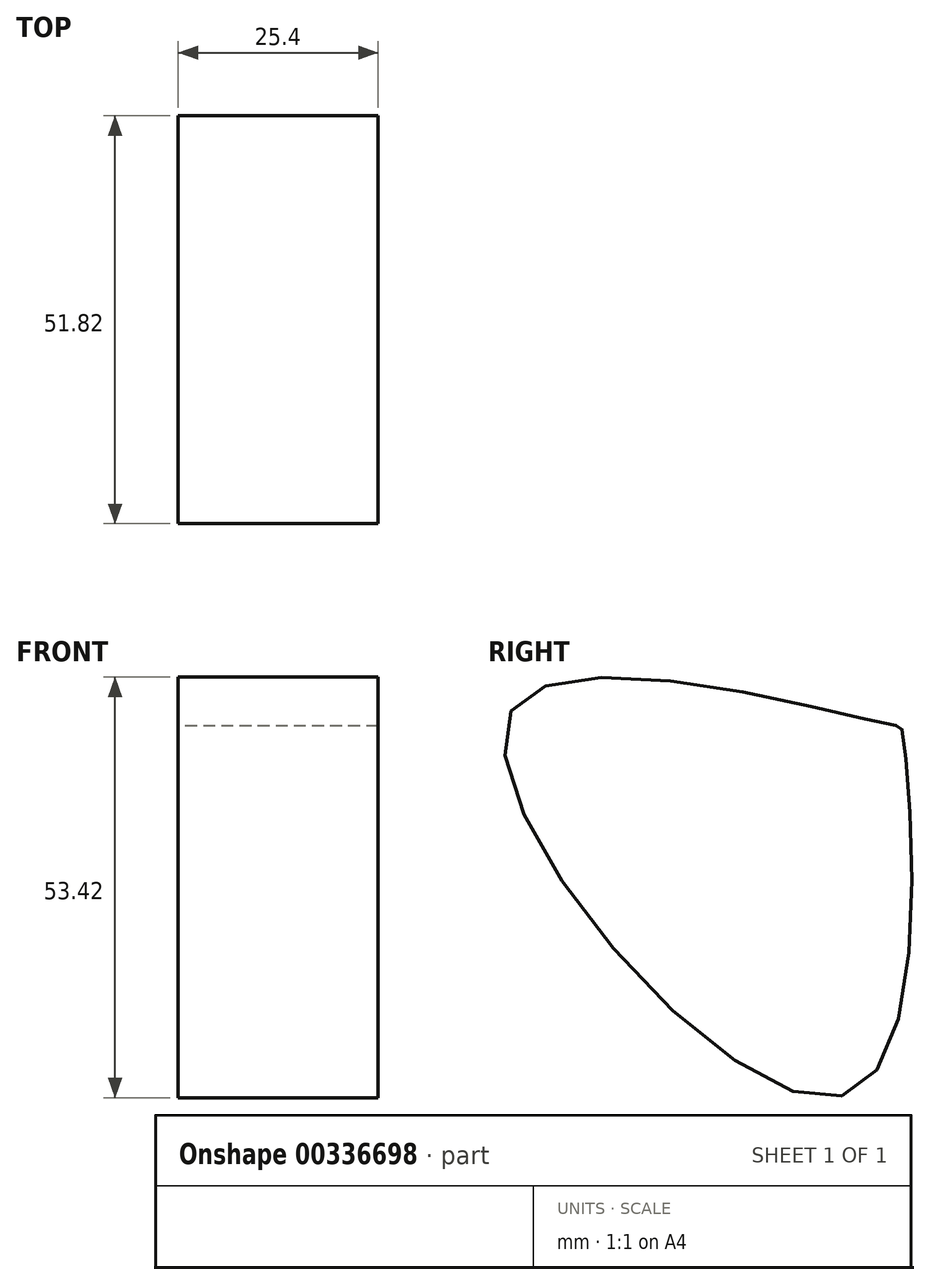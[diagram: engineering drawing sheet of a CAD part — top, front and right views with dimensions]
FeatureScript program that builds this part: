
annotation { "Feature Type Name" : "Feature", "Feature Type Description" : "" }
export const myFeature = defineFeature(function(context is Context, id is Id, definition is map)
    precondition{}
    {
        {
            var Q0;
            Q0=qCreatedBy(makeId("Right.planeOp"),FACE);
            var sketch = newSketch(context, id + "F0", { "sketchPlane" : qUnion([Q0])});
            skFitSpline(sketch, "E0", {"points": [v(-52.6, 48.66) * mm, v(-3.52, 46.77) * mm, v(-2.98, 46.5) * mm, v(-9.76, 0) * mm, v(-52.6, 48.66) * mm]});
            skSolve(sketch);
        }
        {
            var Q0;
            Q0=makeQuery(id+"F0.imprint","IMPRINT",FACE,{"disambiguationData":[TD([[makeQuery(id+"F0.imprint","IMPRINT",EDGE,{"derivedFrom":sQuery(id+"F0.wireOp",EDGE,"E0")}),-1.0]])]});
            extrude(context, id + "F1", {"entities" : qUnion([Q0]), "depth" : 25.4 * mm});
        }
    });
